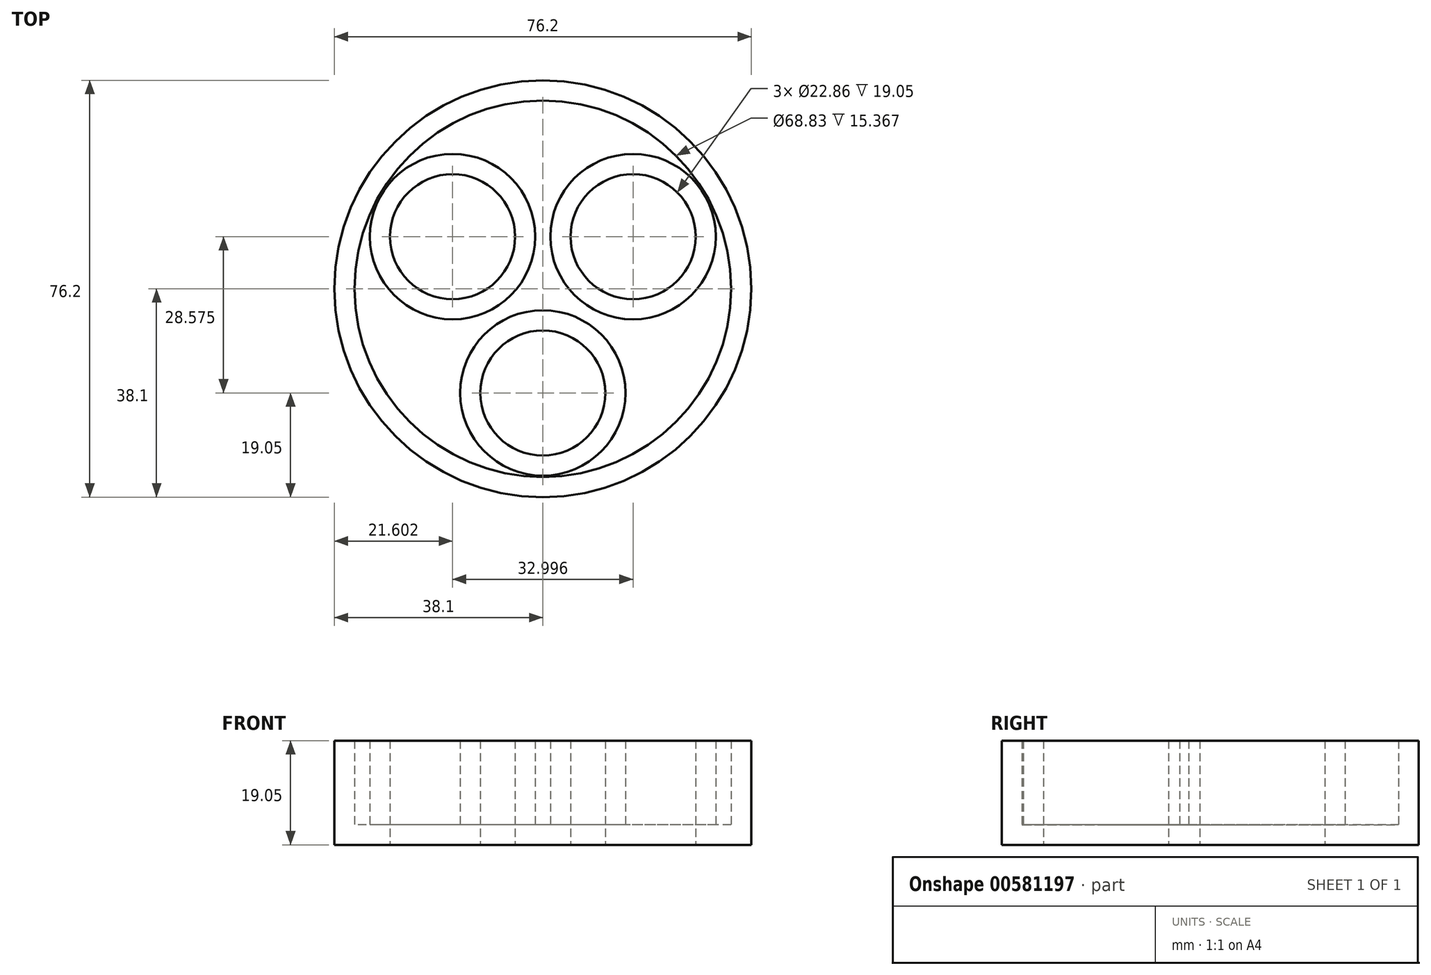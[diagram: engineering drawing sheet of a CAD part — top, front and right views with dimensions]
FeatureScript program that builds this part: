
annotation { "Feature Type Name" : "Feature", "Feature Type Description" : "" }
export const myFeature = defineFeature(function(context is Context, id is Id, definition is map)
    precondition{}
    {
        {
            var Q0;
            Q0=qCreatedBy(makeId("Top.planeOp"),FACE);
            var sketch = newSketch(context, id + "F0", { "sketchPlane" : qUnion([Q0])});
            skCircle(sketch, "E0", {"center": v(0, 0) * mm, "radius": 38.1 * mm});
            skCircle(sketch, "E1", {"center": v(0, -19.05) * mm, "radius": 11.43 * mm});
            skCircle(sketch, "E2.1.0", {"center": v(16.5, 9.52) * mm, "radius": 11.43 * mm});
            skCircle(sketch, "E2.2.0", {"center": v(-16.5, 9.53) * mm, "radius": 11.43 * mm});
            skSolve(sketch);
        }
        {
            var Q0;
            Q0=makeQuery(id+"F0.imprint","IMPRINT",FACE,{"disambiguationData":[TD([[makeQuery(id+"F0.imprint","IMPRINT",EDGE,{"derivedFrom":sQuery(id+"F0.wireOp",EDGE,"E0")}),1.0]])]});
            extrude(context, id + "F1", {"entities" : qUnion([Q0]), "depth" : 19.05 * mm, "offsetDistance" : 25.4 * mm});
        }
        {
            var Q0;
            Q0=makeQuery(id+"F1.opExtrude","CAP_FACE",FACE,{"disambiguationData":[OSD([sQuery(id+"F0.wireOp",EDGE,"E0"),sQuery(id+"F0.wireOp",EDGE,"E1"),sQuery(id+"F0.wireOp",EDGE,"E2.1.0"),sQuery(id+"F0.wireOp",EDGE,"E2.2.0")])],"isStart":false});
            shell(context, id + "F2", {"entities" : qUnion([Q0]), "thickness" : 3.68 * mm});
        }
    });
